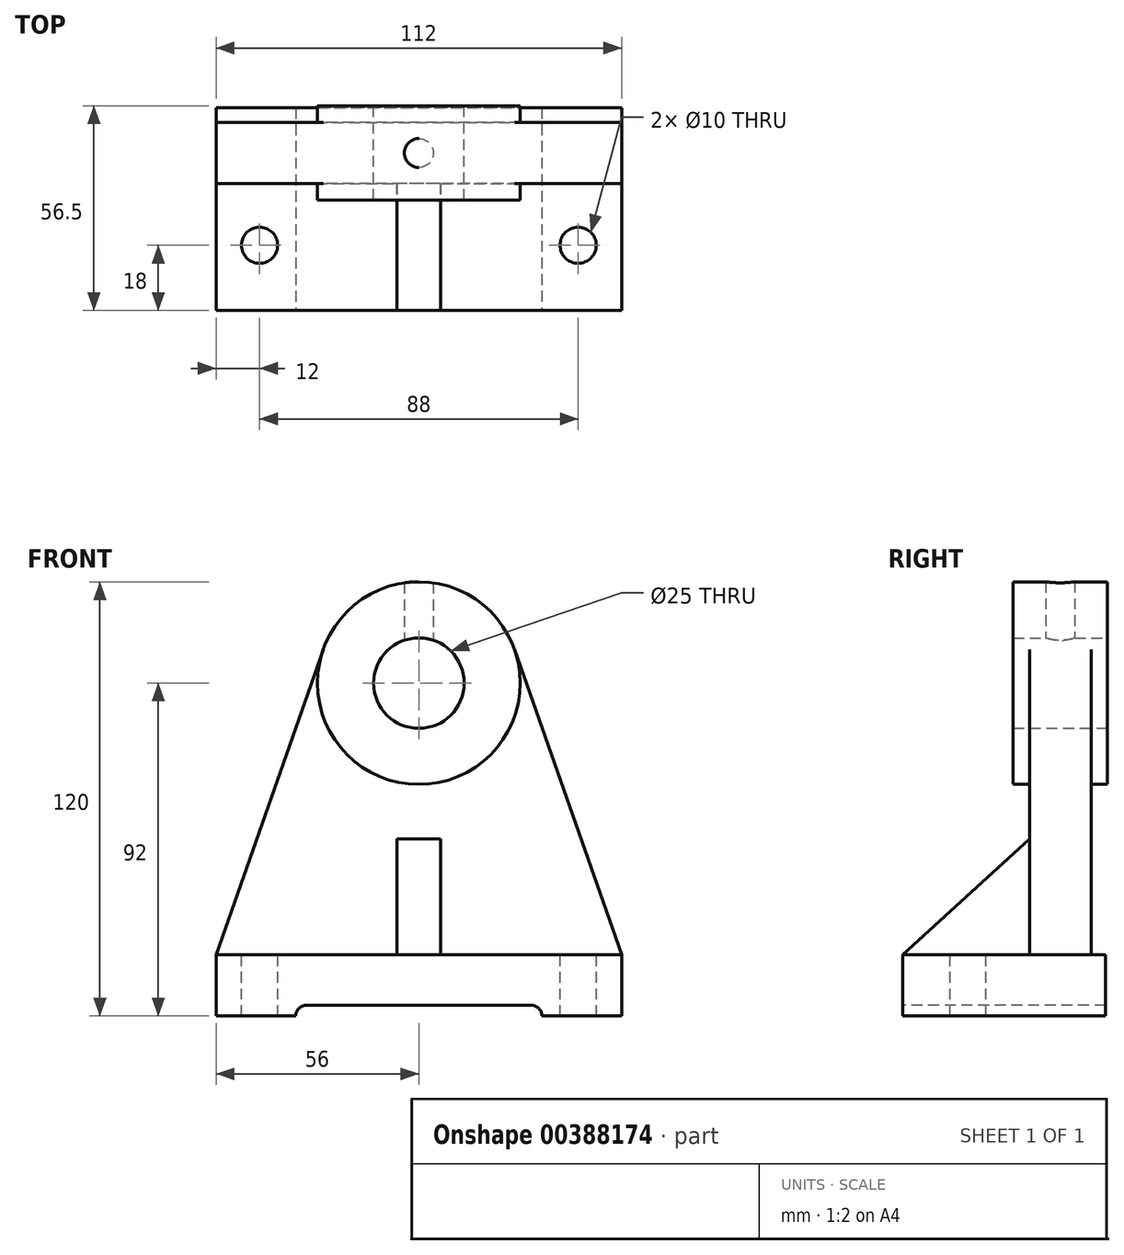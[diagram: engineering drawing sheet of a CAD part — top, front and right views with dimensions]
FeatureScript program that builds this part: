
annotation { "Feature Type Name" : "Feature", "Feature Type Description" : "" }
export const myFeature = defineFeature(function(context is Context, id is Id, definition is map)
    precondition{}
    {
        {
            var Q0;
            Q0=qCreatedBy(makeId("Top.planeOp"),FACE);
            var sketch = newSketch(context, id + "F0", { "sketchPlane" : qUnion([Q0])});
            skLineSegment(sketch, "E0", {"start": v(-56, 28) * mm, "end": v(56, 28) * mm});
            skLineSegment(sketch, "E1", {"start": v(56, 28) * mm, "end": v(56, -28) * mm});
            skLineSegment(sketch, "E2", {"start": v(56, -28) * mm, "end": v(-56, -28) * mm});
            skLineSegment(sketch, "E3", {"start": v(-56, -28) * mm, "end": v(-56, 28) * mm});
            skLineSegment(sketch, "E4", {"start": v(-56, -28) * mm, "end": v(0, 0) * mm, "construction": true});
            skLineSegment(sketch, "E5", {"start": v(0, 0) * mm, "end": v(56, 28) * mm, "construction": true});
            skLineSegment(sketch, "E6", {"start": v(-56, 28) * mm, "end": v(0, 0) * mm, "construction": true});
            skLineSegment(sketch, "E7", {"start": v(56, -28) * mm, "end": v(0, 0) * mm, "construction": true});
            skSolve(sketch);
        }
        {
            var Q0;
            Q0 = qSketchRegion(id + "F0", true);
            extrude(context, id + "F1", {"entities" : qUnion([Q0]), "depth" : 17 * mm});
        }
        {
            var Q0;
            Q0=makeQuery(id+"F1.opExtrude","SWEPT_FACE",FACE,{"disambiguationData":[OSD([sQuery(id+"F0.wireOp",EDGE,"E0")])]});
            cPlane(context, id + "F2", {"entities" : qUnion([Q0]), "cplaneType" : CPlaneType.OFFSET, "offset" : 4 * mm, "oppositeDirection" : true, "width" : 150 * mm, "height" : 150 * mm});
        }
        {
            var Q0;
            Q0=qCreatedBy(id+"F2.planeOp",FACE);
            var sketch = newSketch(context, id + "F3", { "sketchPlane" : qUnion([Q0])});
            skLineSegment(sketch, "E8", {"start": v(-56, 17) * mm, "end": v(-26.42, 101.27) * mm});
            skLineSegment(sketch, "E9", {"start": v(56, 17) * mm, "end": v(26.42, 101.27) * mm});
            skCircle(sketch, "E10", {"center": v(0, 92) * mm, "radius": 28 * mm});
            skCircle(sketch, "E11", {"center": v(0, 92) * mm, "radius": 12.5 * mm});
            skLineSegment(sketch, "E12", {"start": v(56, 17) * mm, "end": v(-56, 17) * mm});
            skSolve(sketch);
        }
        {
            var Q0;
            Q0 = qSketchRegion(id + "F3", true);
            extrude(context, id + "F4", {"entities" : qUnion([Q0]), "operationType" : NewBodyOperationType.ADD, "oppositeDirection" : true, "depth" : 17 * mm});
        }
        {
            var Q0;
            Q0=makeQuery(id+"F4.opExtrude","CAP_FACE",FACE,{"disambiguationData":[OSD([sQuery(id+"F3.wireOp",EDGE,"E8"),sQuery(id+"F3.wireOp",EDGE,"E9"),sQuery(id+"F3.wireOp",EDGE,"E10"),sQuery(id+"F3.wireOp",EDGE,"E11"),sQuery(id+"F3.wireOp",EDGE,"E12")])],"isStart":true});
            cPlane(context, id + "F5", {"entities" : qUnion([Q0]), "cplaneType" : CPlaneType.OFFSET, "offset" : 8.5 * mm, "oppositeDirection" : true, "width" : 150 * mm, "height" : 150 * mm});
        }
        {
            var Q0;
            Q0=qCreatedBy(id+"F5.planeOp",FACE);
            var sketch = newSketch(context, id + "F6", { "sketchPlane" : qUnion([Q0])});
            skCircle(sketch, "E13", {"center": v(0, 92) * mm, "radius": 28 * mm});
            skSolve(sketch);
        }
        {
            var Q0;
            Q0 = qSketchRegion(id + "F6", true);
            extrude(context, id + "F7", {"entities" : qUnion([Q0]), "operationType" : NewBodyOperationType.ADD, "endBound" : BoundingType.SYMMETRIC, "depth" : 26 * mm});
        }
        {
            var Q0;
            Q0=makeQuery(id+"F3.imprint","IMPRINT",FACE,{"disambiguationData":[TD([[makeQuery(id+"F3.imprint","IMPRINT",EDGE,{"derivedFrom":sQuery(id+"F3.wireOp",EDGE,"E11")}),1.0]])]});
            extrude(context, id + "F8", {"entities" : qUnion([Q0]), "operationType" : NewBodyOperationType.REMOVE, "endBound" : BoundingType.SYMMETRIC, "oppositeDirection" : true, "depth" : 50 * mm});
        }
        {
            var Q0;
            Q0=qCreatedBy(makeId("Top.planeOp"),FACE);
            cPlane(context, id + "F9", {"entities" : qUnion([Q0]), "cplaneType" : CPlaneType.OFFSET, "offset" : 92 * mm, "width" : 150 * mm, "height" : 150 * mm});
        }
        {
            var Q0;
            Q0=qCreatedBy(id+"F9.planeOp",FACE);
            var sketch = newSketch(context, id + "F10", { "sketchPlane" : qUnion([Q0])});
            skCircle(sketch, "E14", {"center": v(0, 15.5) * mm, "radius": 4 * mm});
            skSolve(sketch);
        }
        {
            var Q0;
            Q0 = qSketchRegion(id + "F10", true);
            extrude(context, id + "F11", {"entities" : qUnion([Q0]), "operationType" : NewBodyOperationType.REMOVE, "endBound" : BoundingType.THROUGH_ALL, "depth" : 25 * mm});
        }
        {
            var Q0;
            {var subQ0=sQuery(id+"F0.wireOp",EDGE,"E3");var subQ2=sQuery(id+"F0.wireOp",EDGE,"E2");var subQ3=sQuery(id+"F0.wireOp",EDGE,"E1");Q0=makeQuery(id+"F4.boolean.opBoolean","SPLIT",FACE,{"disambiguationData":[TD([makeQuery(id+"F1.opExtrude","SWEPT_FACE",FACE,{"disambiguationData":[OSD([subQ2])]})])],"derivedFrom":makeQuery(id+"F1.opExtrude","CAP_FACE",FACE,{"disambiguationData":[OSD([sQuery(id+"F0.wireOp",EDGE,"E0"),subQ3,subQ2,subQ0])],"isStart":false})});}
            var sketch = newSketch(context, id + "F12", { "sketchPlane" : qUnion([Q0])});
            skCircle(sketch, "E15", {"center": v(-44, -10) * mm, "radius": 5 * mm});
            skCircle(sketch, "E16", {"center": v(44, -10) * mm, "radius": 5 * mm});
            skLineSegment(sketch, "E17", {"start": v(-44, -10) * mm, "end": v(0, 0) * mm, "construction": true});
            skLineSegment(sketch, "E18", {"start": v(0, 0) * mm, "end": v(44, -10) * mm, "construction": true});
            skSolve(sketch);
        }
        {
            var Q0;
            Q0 = qSketchRegion(id + "F12", true);
            extrude(context, id + "F13", {"entities" : qUnion([Q0]), "operationType" : NewBodyOperationType.REMOVE, "endBound" : BoundingType.THROUGH_ALL, "oppositeDirection" : true, "depth" : 25 * mm});
        }
        {
            var Q0;
            Q0=makeQuery(id+"F1.opExtrude","SWEPT_FACE",FACE,{"disambiguationData":[OSD([sQuery(id+"F0.wireOp",EDGE,"E1")])]});
            cPlane(context, id + "F14", {"entities" : qUnion([Q0]), "cplaneType" : CPlaneType.OFFSET, "offset" : 56 * mm, "oppositeDirection" : true, "width" : 150 * mm, "height" : 150 * mm});
        }
        {
            var Q0;
            Q0=qCreatedBy(id+"F14.planeOp",FACE);
            var sketch = newSketch(context, id + "F15", { "sketchPlane" : qUnion([Q0])});
            skLineSegment(sketch, "E19", {"start": v(7, 49) * mm, "end": v(-28, 17) * mm});
            skLineSegment(sketch, "E20", {"start": v(-28, 17) * mm, "end": v(7, 17) * mm});
            skLineSegment(sketch, "E21", {"start": v(7, 17) * mm, "end": v(7, 49) * mm});
            skSolve(sketch);
        }
        {
            var Q0;
            Q0 = qSketchRegion(id + "F15", true);
            extrude(context, id + "F16", {"entities" : qUnion([Q0]), "operationType" : NewBodyOperationType.ADD, "endBound" : BoundingType.SYMMETRIC, "depth" : 12 * mm});
        }
        {
            var Q0;
            Q0=makeQuery(id+"F1.opExtrude","SWEPT_FACE",FACE,{"disambiguationData":[OSD([sQuery(id+"F0.wireOp",EDGE,"E2")])]});
            var sketch = newSketch(context, id + "F17", { "sketchPlane" : qUnion([Q0])});
            skArc(sketch, "E22", {"start": v(-31, 3) * mm, "mid": v(-34, 0) * mm, "end": v(-31, -3) * mm});
            skArc(sketch, "E23", {"start": v(31, -3) * mm, "mid": v(34, 0) * mm, "end": v(31, 3) * mm});
            skLineSegment(sketch, "E24", {"start": v(-31, 3) * mm, "end": v(31, 3) * mm});
            skLineSegment(sketch, "E25", {"start": v(-31, -3) * mm, "end": v(31, -3) * mm});
            skLineSegment(sketch, "E26", {"start": v(-34, 0) * mm, "end": v(34, 0) * mm, "construction": true});
            skPoint(sketch, "E26.startSnap0", {"position": v(-34, 0) * mm});
            skSolve(sketch);
        }
        {
            var Q0;
            Q0 = qSketchRegion(id + "F17", true);
            extrude(context, id + "F18", {"entities" : qUnion([Q0]), "operationType" : NewBodyOperationType.REMOVE, "endBound" : BoundingType.THROUGH_ALL, "oppositeDirection" : true, "depth" : 25 * mm});
        }
    });
